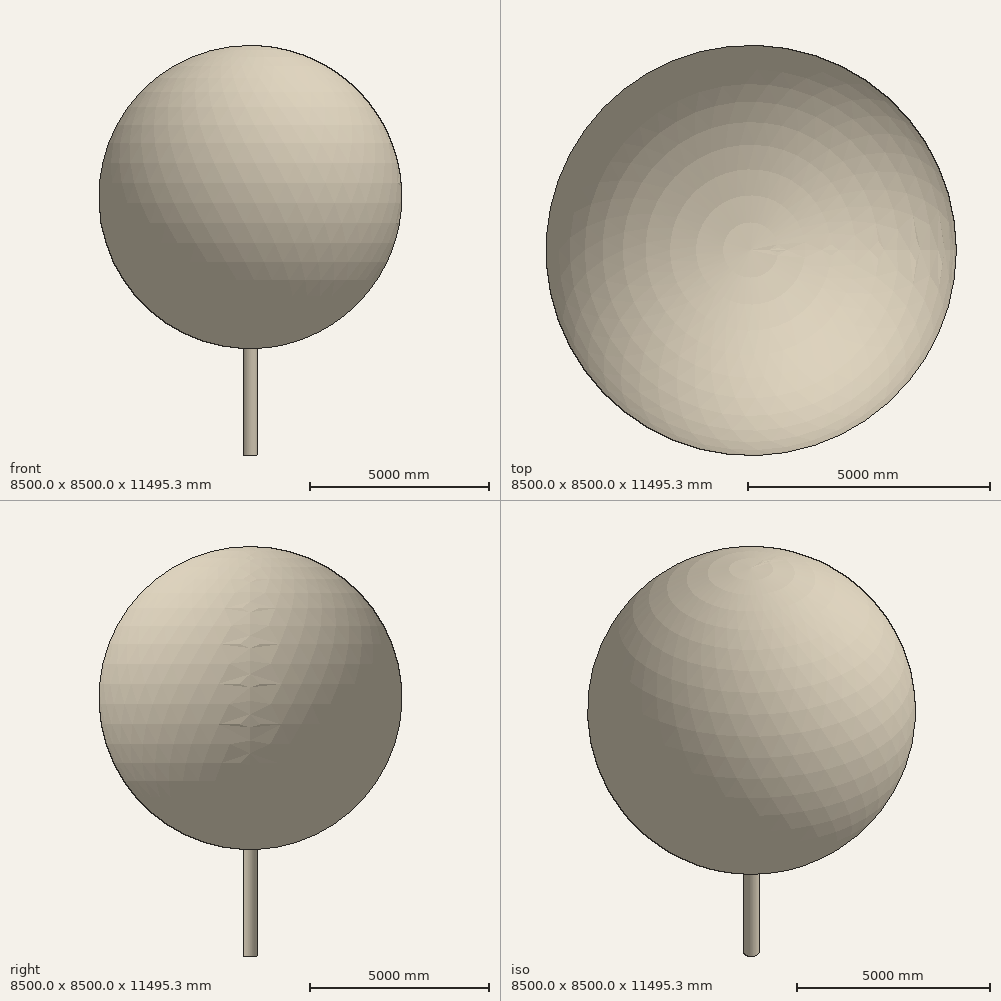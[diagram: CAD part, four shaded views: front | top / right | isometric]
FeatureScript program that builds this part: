
annotation { "Feature Type Name" : "Feature", "Feature Type Description" : "" }
export const myFeature = defineFeature(function(context is Context, id is Id, definition is map)
    precondition{}
    {
        {
            var Q0;
            Q0=qCreatedBy(makeId("Front.planeOp"),FACE);
            var sketch = newSketch(context, id + "F0", { "sketchPlane" : qUnion([Q0])});
            skArc(sketch, "E0", {"start": v(200, -4245.3) * mm, "mid": v(4248.82, 100.03) * mm, "end": v(0, 4250) * mm});
            skLineSegment(sketch, "E1", {"start": v(0, -4245.3) * mm, "end": v(200, -4245.3) * mm});
            skLineSegment(sketch, "E2", {"start": v(0, -4245.3) * mm, "end": v(0, 4250) * mm});
            skSolve(sketch);
        }
        {
            var Q0;
            Q0=qSketchRegion(id+"F0",true);
            var Q1;
            Q1=sQuery(id+"F0.wireOp",EDGE,"E2");
            revolve(context, id + "F1", {"entities" : qUnion([Q0]), "axis" : qUnion([Q1]), "revolveType" : RevolveType.FULL});
        }
        {
            var Q0;
            Q0=makeQuery(id+"F1.opRevolve","SWEPT_FACE",FACE,{"disambiguationData":[OSD([sQuery(id+"F0.wireOp",EDGE,"E1")])]});
            var sketch = newSketch(context, id + "F2", { "sketchPlane" : qUnion([Q0])});
            skCircle(sketch, "E3.0", {"center": v(0, 0) * mm, "radius": 200 * mm});
            skSolve(sketch);
        }
        {
            var Q0;
            Q0=qSketchRegion(id+"F2",true);
            extrude(context, id + "F3", {"entities" : qUnion([Q0]), "depth" : 3000 * mm});
        }
    });
